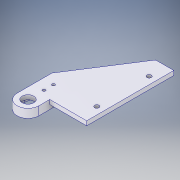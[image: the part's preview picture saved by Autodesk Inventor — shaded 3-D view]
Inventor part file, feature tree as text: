
AUTODESK INVENTOR PART (.ipt)
format: ipt  version: 2017 (Build 210142000, 142)  size: 155,648 bytes
history: native  units: in
note: dims shown in document units (in); Inventor stores cm internally (conversion verified against a paired STEP export)
features: extrude x2, sketch x2, projected_geometry x1
ambient origin geometry x8: Origin, YZ Plane, XZ Plane, XY Plane, X Axis, Y Axis, Z Axis, Center Point
bodies: Solid1 (feature_tree)
feature tree (5):
  extrude  "Extrusion1"  TaperAngle=90.0deg  [1 undecoded]
  extrude  "Extrusion3"  Depth=1.0in
  sketch  "Sketch3"  dims[d6=2.3622in d7=90.0deg]
  sketch  "Sketch6"  dims[d8=0.4929in d9=1.0in d10=0.2953in d11=0.5906in d13=0.9456in d14=0.1181in d15=0.0in d18=0.1969in d19=0.4724in d20=0.4724in d21=0.1181in d22=0.1181in d25=0.315in d26=0.4335in d27=0.2562in d28=0.0787in d29=0.0787in d31=0.4331in d32=0.0591in d33=0.2362in d34=0.1181in d35=0.2362in d36=0.0in]
  projected_geometry  "Projected Loop3"
note: 1 required parameter value undecoded (feature->parameter linkage not recoverable at this tier; creation-order binding heuristic only, values carry confidence <= 0.55)
